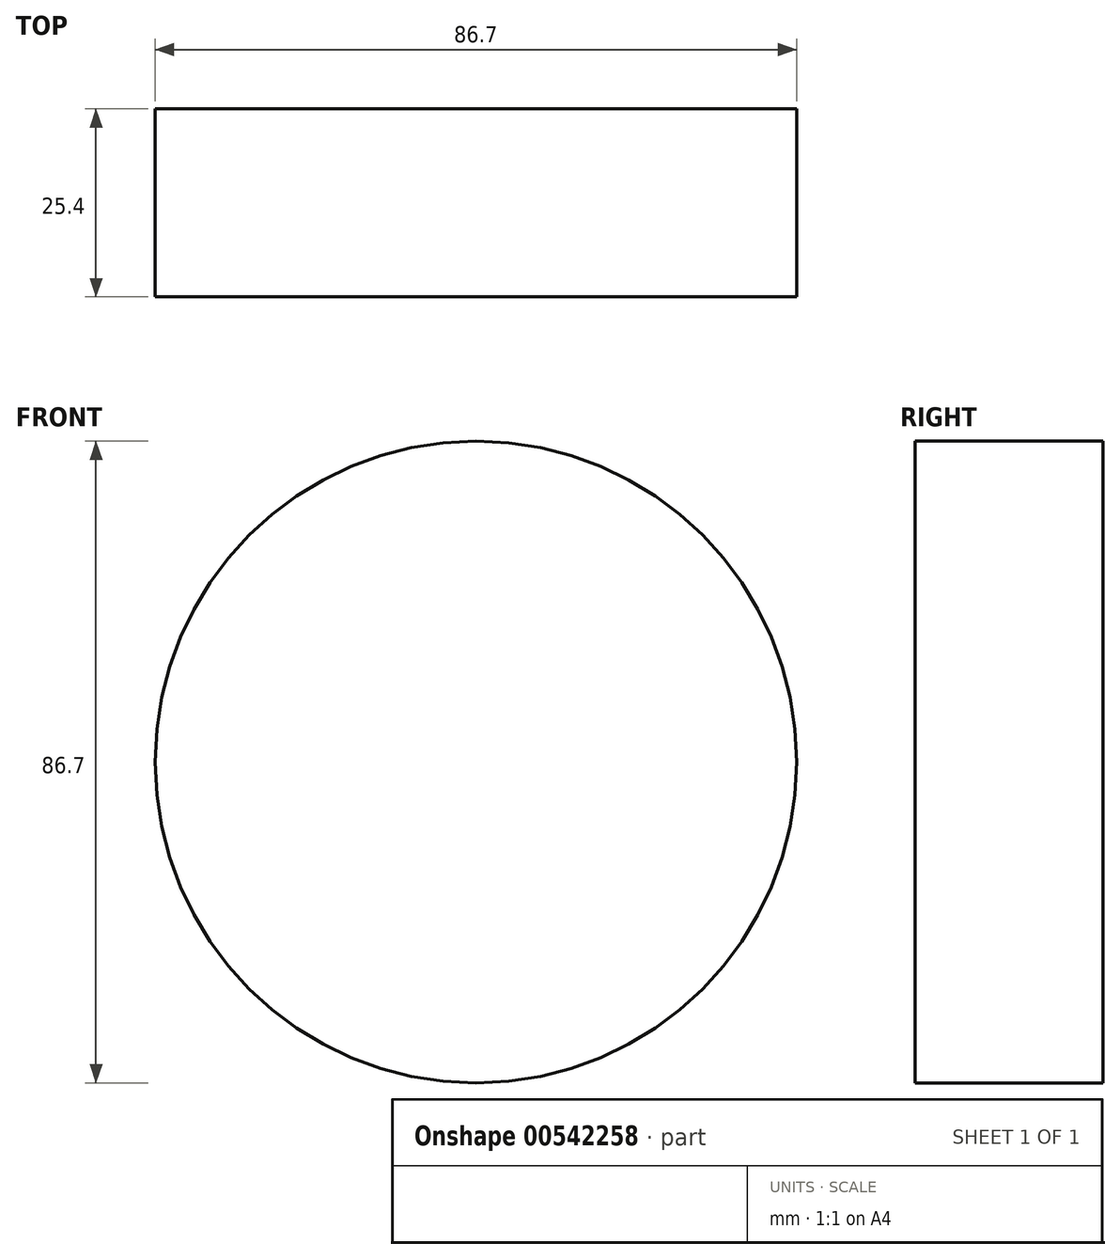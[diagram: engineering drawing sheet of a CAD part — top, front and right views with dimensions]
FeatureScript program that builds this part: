
annotation { "Feature Type Name" : "Feature", "Feature Type Description" : "" }
export const myFeature = defineFeature(function(context is Context, id is Id, definition is map)
    precondition{}
    {
        {
            var Q0;
            Q0=qCreatedBy(makeId("Front.planeOp"),FACE);
            var sketch = newSketch(context, id + "F0", { "sketchPlane" : qUnion([Q0])});
            skCircle(sketch, "E0", {"center": v(0, 0) * mm, "radius": 43.35 * mm});
            skSolve(sketch);
        }
        {
            var Q0;
            Q0=sQuery(id+"F0.wireOp",EDGE,"E0");
            extrude(context, id + "F1", {"bodyType" : ExtendedToolBodyType.SURFACE, "surfaceEntities" : qUnion([Q0]), "depth" : 25.4 * mm, "offsetDistance" : 25.4 * mm});
        }
    });
